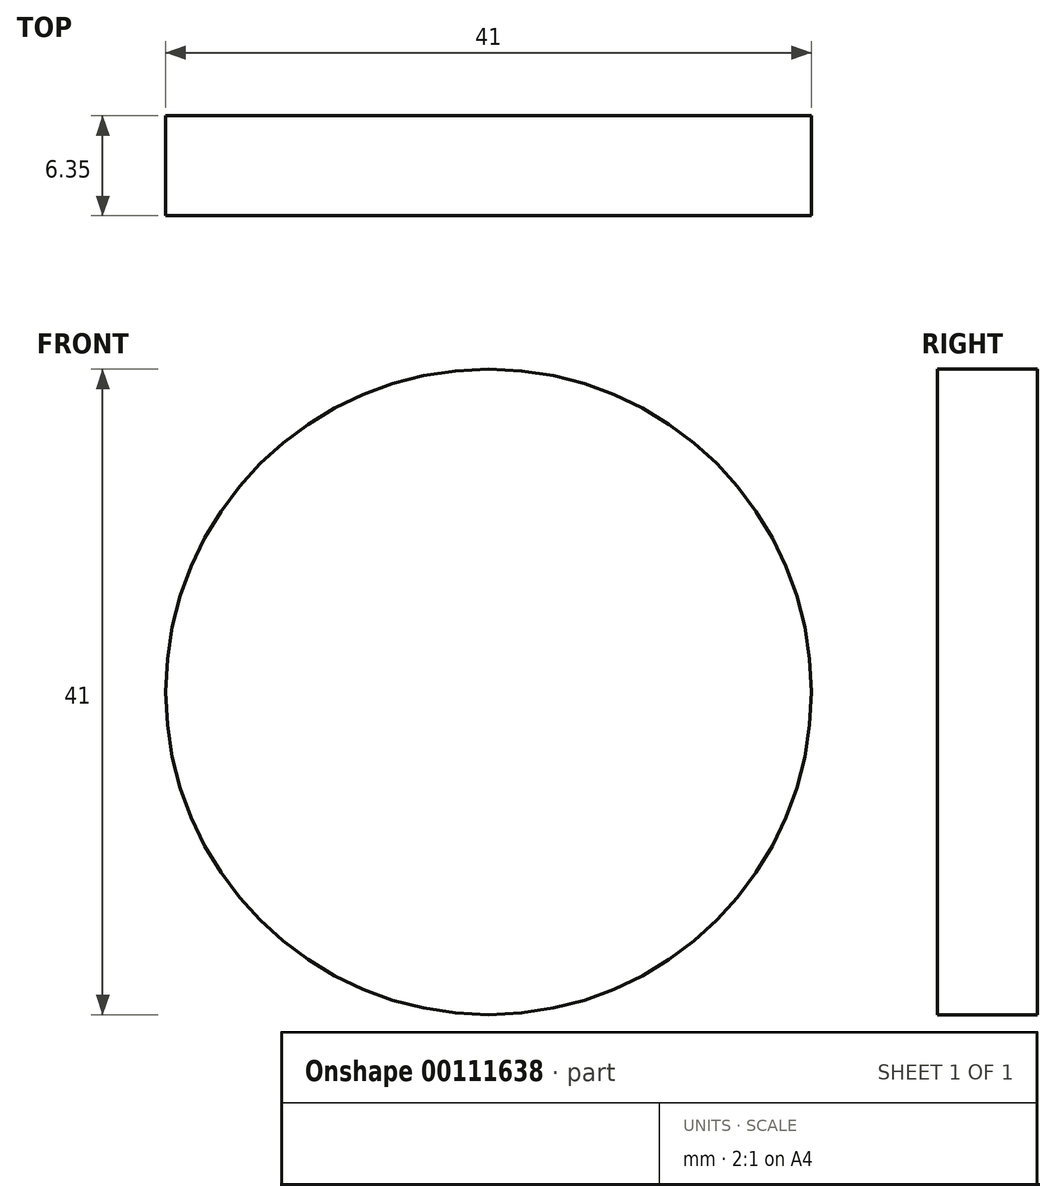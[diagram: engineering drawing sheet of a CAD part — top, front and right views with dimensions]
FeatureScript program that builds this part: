
annotation { "Feature Type Name" : "Feature", "Feature Type Description" : "" }
export const myFeature = defineFeature(function(context is Context, id is Id, definition is map)
    precondition{}
    {
        {
            var Q0;
            Q0=qCreatedBy(makeId("Front.planeOp"),FACE);
            var sketch = newSketch(context, id + "F0", { "sketchPlane" : qUnion([Q0])});
            skCircle(sketch, "E0", {"center": v(0, 0) * mm, "radius": 20.5 * mm});
            skLineSegment(sketch, "E1", {"start": v(-20.5, 0) * mm, "end": v(20.5, 0) * mm});
            skSolve(sketch);
        }
        {
            var Q0;
            Q0 = qSketchRegion(id + "F0", true);
            extrude(context, id + "F1", {"entities" : qUnion([Q0]), "depth" : 6.35 * mm});
        }
    });
